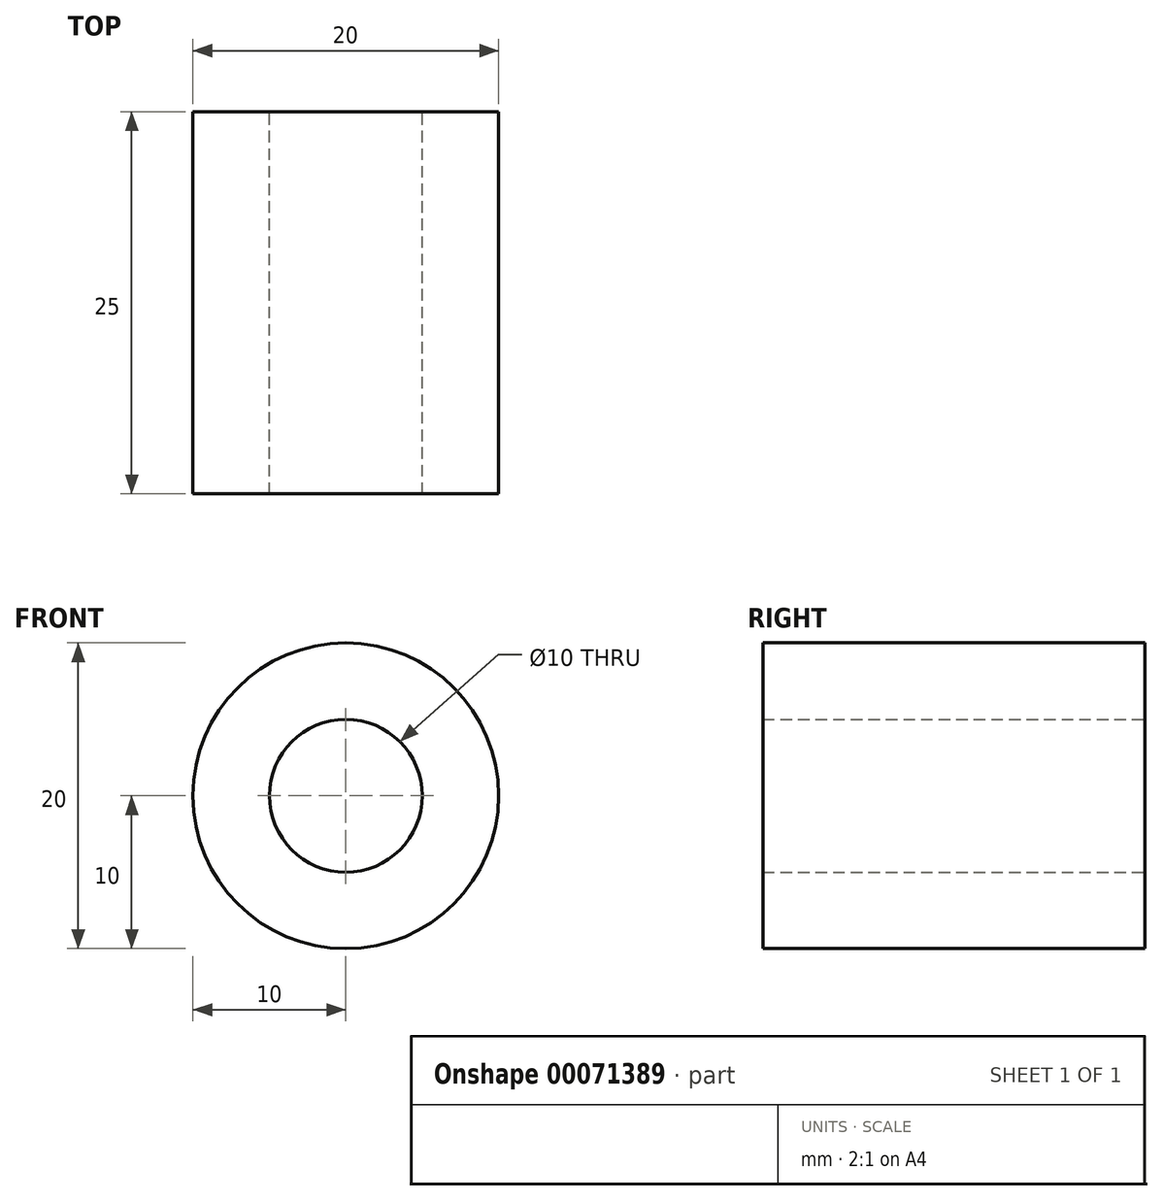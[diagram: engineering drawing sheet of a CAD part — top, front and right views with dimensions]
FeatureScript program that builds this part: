
annotation { "Feature Type Name" : "Feature", "Feature Type Description" : "" }
export const myFeature = defineFeature(function(context is Context, id is Id, definition is map)
    precondition{}
    {
        {
            var Q0;
            Q0=qCreatedBy(makeId("Front.planeOp"),FACE);
            var sketch = newSketch(context, id + "F0", { "sketchPlane" : qUnion([Q0])});
            skCircle(sketch, "E0", {"center": v(0, 0) * mm, "radius": 10 * mm});
            skCircle(sketch, "E1", {"center": v(0, 0) * mm, "radius": 5 * mm});
            skSolve(sketch);
        }
        {
            var Q0;
            Q0=makeQuery(id+"F0.imprint","IMPRINT",FACE,{"disambiguationData":[TD([[makeQuery(id+"F0.imprint","IMPRINT",EDGE,{"derivedFrom":sQuery(id+"F0.wireOp",EDGE,"E0")}),1.0]])]});
            extrude(context, id + "F1", {"entities" : qUnion([Q0]), "depth" : 25 * mm});
        }
    });
